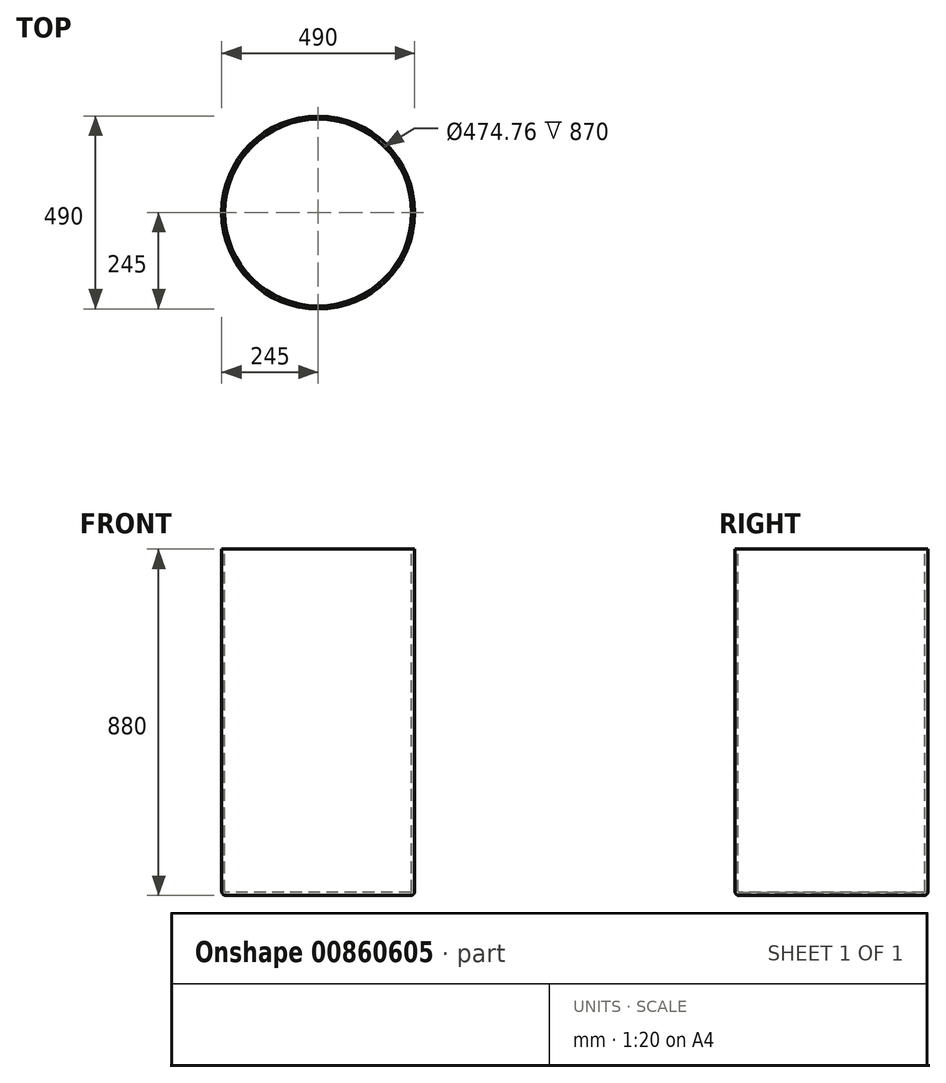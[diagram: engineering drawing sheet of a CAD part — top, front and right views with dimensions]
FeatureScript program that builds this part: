
annotation { "Feature Type Name" : "Feature", "Feature Type Description" : "" }
export const myFeature = defineFeature(function(context is Context, id is Id, definition is map)
    precondition{}
    {
        {
            var Q0;
            Q0=qCreatedBy(makeId("Top.planeOp"),FACE);
            var sketch = newSketch(context, id + "F0", { "sketchPlane" : qUnion([Q0])});
            skCircle(sketch, "E0", {"center": v(0, 0) * mm, "radius": 245 * mm});
            skSolve(sketch);
        }
        {
            var Q0;
            Q0 = qSketchRegion(id + "F0", true);
            extrude(context, id + "F1", {"entities" : qUnion([Q0]), "oppositeDirection" : true, "depth" : 880 * mm, "offsetDistance" : 25.4 * mm});
        }
        {
            var Q0;
            Q0=makeQuery(id+"F1.opExtrude","CAP_EDGE",EDGE,{"disambiguationData":[OSD([sQuery(id+"F0.wireOp",EDGE,"E0")])],"isStart":false});
            fillet(context, id + "F2", {"entities" : qUnion([Q0]), "radius" : 10 * mm, "tangentPropagation" : true, "allowEdgeOverflow" : false});
        }
        {
            var Q0;
            Q0=makeQuery(id+"F1.opExtrude","CAP_FACE",FACE,{"disambiguationData":[OSD([sQuery(id+"F0.wireOp",EDGE,"E0")])],"isStart":true});
            shell(context, id + "F3", {"entities" : qUnion([Q0]), "thickness" : 7.62 * mm});
        }
    });
